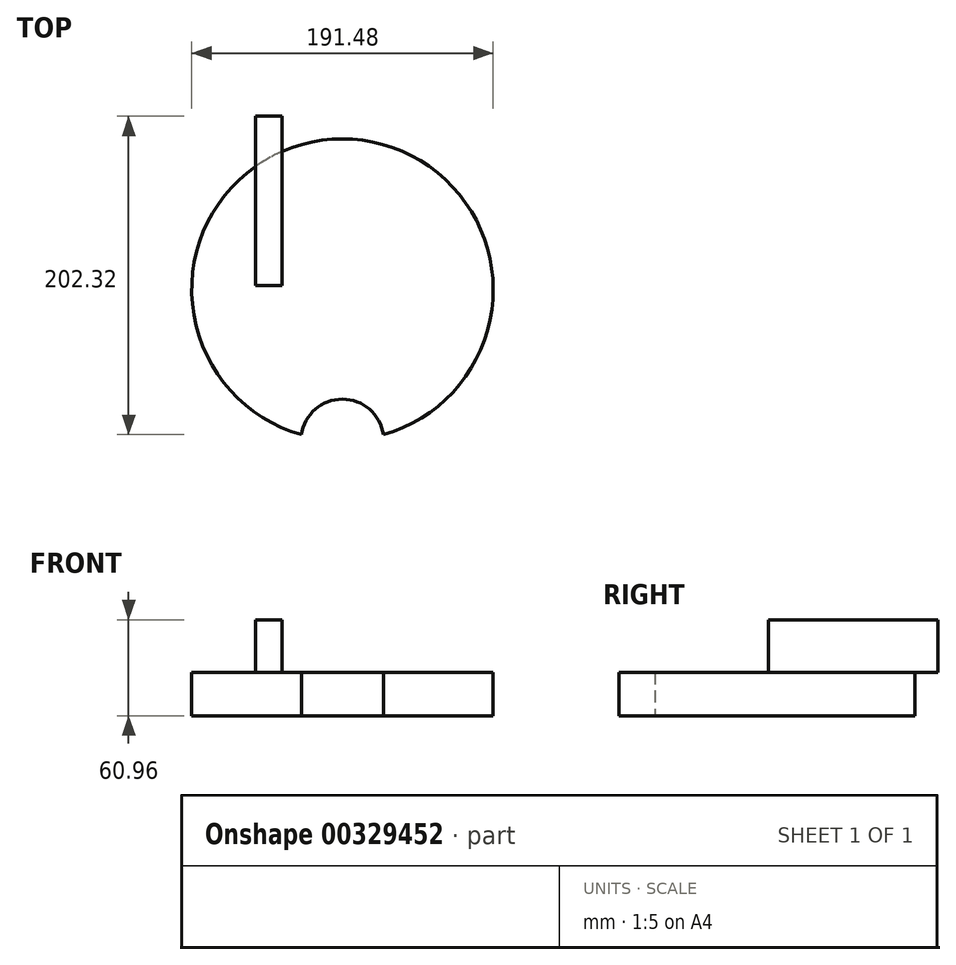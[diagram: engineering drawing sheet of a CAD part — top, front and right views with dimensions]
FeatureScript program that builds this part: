
annotation { "Feature Type Name" : "Feature", "Feature Type Description" : "" }
export const myFeature = defineFeature(function(context is Context, id is Id, definition is map)
    precondition{}
    {
        {
            var Q0;
            Q0=qCreatedBy(makeId("Front.planeOp"),FACE);
            var sketch = newSketch(context, id + "F0", { "sketchPlane" : qUnion([Q0])});
            skCircle(sketch, "E0", {"center": v(0, 0) * mm, "radius": 14.63 * mm});
            skCircle(sketch, "E1", {"center": v(0, 0) * mm, "radius": 39.55 * mm});
            skCircle(sketch, "E2", {"center": v(6.87, 38.95) * mm, "radius": 16.1 * mm});
            skCircle(sketch, "E3", {"center": v(0, 0) * mm, "radius": 79.67 * mm});
            skCircle(sketch, "E4", {"center": v(0, 0) * mm, "radius": 125.76 * mm});
            skCircle(sketch, "E5", {"center": v(-77.09, -20.14) * mm, "radius": 25.82 * mm});
            skCircle(sketch, "E6", {"center": v(-77.09, -20.14) * mm, "radius": 19.54 * mm});
            skSolve(sketch);
        }
        {
            var Q0;
            Q0=sQuery(id+"F0.wireOp",EDGE,"E3");
            extrude(context, id + "F1", {"bodyType" : ToolBodyType.SURFACE, "surfaceEntities" : qUnion([Q0]), "depth" : 25.4 * mm});
        }
        {
            var Q0;
            Q0=qCreatedBy(makeId("Top.planeOp"),FACE);
            var sketch = newSketch(context, id + "F2", { "sketchPlane" : qUnion([Q0])});
            skCircle(sketch, "E7", {"center": v(0, -2.52) * mm, "radius": 95.74 * mm});
            skCircle(sketch, "E8", {"center": v(-8.62, -127.73) * mm, "radius": 27.03 * mm});
            skCircle(sketch, "E9", {"center": v(0, -98.26) * mm, "radius": 26.22 * mm});
            skSolve(sketch);
        }
        {
            var Q0;
            {var subQ0=sQuery(id+"F2.wireOp",EDGE,"E9");var subQ1=sQuery(id+"F2.wireOp",EDGE,"E7");var subQ2=makeQuery(id+"F2.imprint","INTERSECT",VERTEX,{"disambiguationData":[OD(0.0)],"derivedFrom":[subQ1,subQ0]});Q0=makeQuery(id+"F2.imprint","IMPRINT",FACE,{"disambiguationData":[TD([[makeQuery(id+"F2.imprint","IMPRINT",EDGE,{"disambiguationData":[TD([[subQ2,1.0]])],"derivedFrom":subQ1}),1.0]])]});}
            extrude(context, id + "F3", {"entities" : qUnion([Q0]), "depth" : 27.43 * mm});
        }
        {
            var Q0;
            Q0=makeQuery(id+"F3.opExtrude","CAP_FACE",FACE,{"disambiguationData":[OSD([sQuery(id+"F2.wireOp",EDGE,"E7"),sQuery(id+"F2.wireOp",EDGE,"E9")])],"isStart":false});
            var sketch = newSketch(context, id + "F4", { "sketchPlane" : qUnion([Q0])});
            skLineSegment(sketch, "E10.bottom", {"start": v(-38.3, 0) * mm, "end": v(-55.06, 0) * mm});
            skLineSegment(sketch, "E10.top", {"start": v(-38.3, 107.65) * mm, "end": v(-55.06, 107.65) * mm});
            skLineSegment(sketch, "E10.left", {"start": v(-38.3, 0) * mm, "end": v(-38.3, 107.65) * mm});
            skLineSegment(sketch, "E10.right", {"start": v(-55.06, 0) * mm, "end": v(-55.06, 107.65) * mm});
            skSolve(sketch);
        }
        {
            var Q0;
            {var subQ0=sQuery(id+"F4.wireOp",EDGE,"E10.top");Q0=makeQuery(id+"F4.imprint","IMPRINT",FACE,{"disambiguationData":[TD([[makeQuery(id+"F4.imprint","IMPRINT",EDGE,{"derivedFrom":subQ0}),1.0]])]});}
            var Q1;
            {var subQ0=sQuery(id+"F4.wireOp",EDGE,"E10.bottom");Q1=makeQuery(id+"F4.imprint","IMPRINT",FACE,{"disambiguationData":[TD([[makeQuery(id+"F4.imprint","IMPRINT",EDGE,{"derivedFrom":subQ0}),-1.0]])]});}
            extrude(context, id + "F5", {"entities" : qUnion([Q0, Q1]), "operationType" : NewBodyOperationType.ADD, "depth" : 33.53 * mm});
        }
    });
